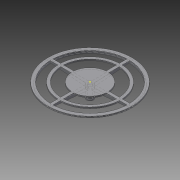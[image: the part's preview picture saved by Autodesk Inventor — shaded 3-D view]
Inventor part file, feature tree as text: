
AUTODESK INVENTOR PART (.ipt)
format: ipt  version: 2015 (Build 190159000, 159)  size: 297,984 bytes
history: native  units: mm
features: sketch x10, chamfer x9, extrude x8, hole x1
ambient origin geometry x8: Origin, YZ Plane, XZ Plane, XY Plane, X Axis, Y Axis, Z Axis, Center Point
bodies: Solid1 (feature_tree)
feature tree (28):
  extrude  "Extrusion1"  Depth=10.0mm
  extrude  "Extrusion2"  Depth=20.0mm
  extrude  "Extrusion3"  Depth=2.0mm
  chamfer  "Chamfer1"  Distance=2.7mm
  chamfer  "Chamfer2"  Distance=1.5mm
  chamfer  "Chamfer3"  Distance=2.0mm Angle=45.0deg
  chamfer  "Chamfer4"  Distance=2.0mm Angle=45.0deg
  hole  "Hole1"  [1 undecoded]
  sketch  "Sketch5"  dims[d9=2.0mm]
  extrude  "Extrusion4"  Depth=2.0mm TaperAngle=45.0deg
  chamfer  "Chamfer5"  Distance=10.0mm
  extrude  "Extrusion5"  Depth=55.0mm
  extrude  "Extrusion6"  Depth=55.0mm
  chamfer  "Chamfer6"  Distance=55.0mm
  chamfer  "Chamfer7"  Distance=55.0mm
  chamfer  "Chamfer8"  Distance=2.0mm
  chamfer  "Chamfer9"  Distance=2.0mm Angle=45.0deg
  extrude  "Extrusion7"  Depth=5.0mm
  extrude  "Extrusion8"  Depth=2.0mm
  sketch  "Sketch1"  dims[d0=5.2mm d1=10.0mm]
  sketch  "Sketch2"  dims[d2=20.0mm d3=0.0mm d4=50.0mm]
  sketch  "Sketch3"  dims[d5=2.0mm d6=0.0mm d7=2.0mm]
  sketch  "Sketch4"  dims[d8=2.0mm]
  sketch  "Sketch6"  dims[d10=2.0mm]
  sketch  "Sketch7"  dims[d11=22.0mm]
  sketch  "Sketch8"  dims[d12=22.0mm]
  sketch  "Sketch9"  dims[d13=22.0mm]
  sketch  "Sketch10"  dims[d14=22.0mm d15=2.7mm d16=1.5mm d17=0.0mm d18=1.5mm d19=2.0mm d20=45.0deg d21=1.5mm d22=2.0mm d23=45.0deg d24=1.5mm d25=2.0mm d26=45.0deg d27=1.5mm d28=2.0mm d29=45.0deg d30=10.0mm d31=3.0mm d32=6.0mm d33=4.0mm d34=2.0mm d35=90.0deg d36=8.0mm d37=20.594885mm d38=55.0mm d39=55.0mm d40=55.0mm d41=55.0mm d42=2.0mm d43=0.0mm d44=1.5mm d45=2.0mm d46=45.0deg d47=5.0mm d48=120.0mm d49=2.0mm d50=0.0mm d51=5.0mm d52=0.0mm d53=55.0mm d54=5.0mm d55=4.363323mm d56=55.0mm d57=5.0mm d58=4.363323mm d59=55.0mm d60=5.0mm d61=4.363323mm d62=55.0mm d63=5.0mm d64=4.363323mm d65=80.0mm d66=88.0mm d67=2.0mm d68=0.0mm d69=110.0mm d70=2.0mm d71=2.0mm d72=0.0mm]
note: 1 required parameter value undecoded (feature->parameter linkage not recoverable at this tier; creation-order binding heuristic only, values carry confidence <= 0.55)
